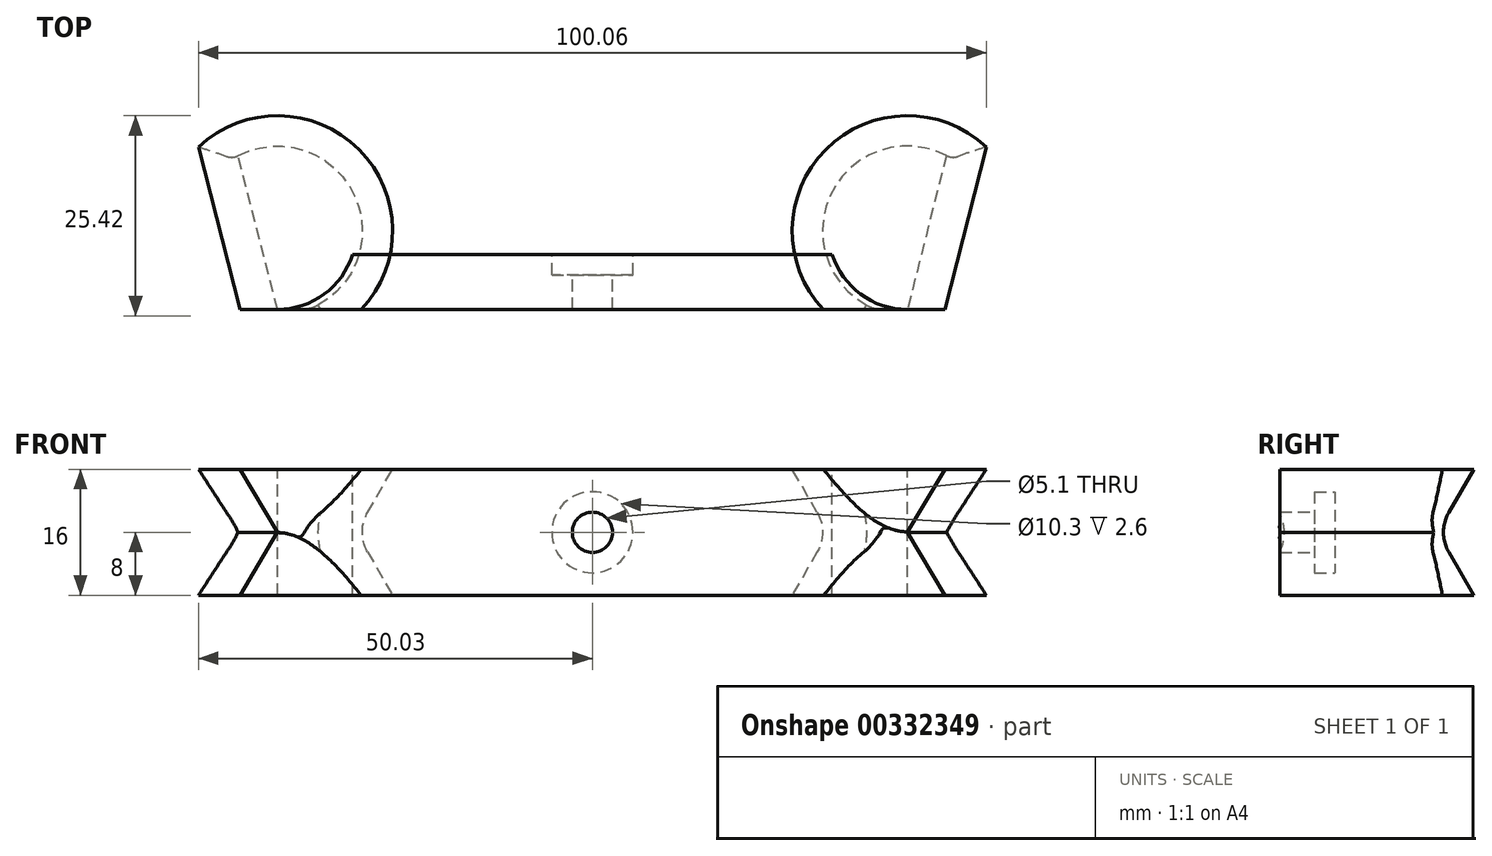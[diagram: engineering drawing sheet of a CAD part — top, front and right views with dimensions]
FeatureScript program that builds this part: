
annotation { "Feature Type Name" : "Feature", "Feature Type Description" : "" }
export const myFeature = defineFeature(function(context is Context, id is Id, definition is map)
    precondition{}
    {
        {
            var Q0;
            Q0=qCreatedBy(makeId("Top.planeOp"),FACE);
            var sketch = newSketch(context, id + "F0", { "sketchPlane" : qUnion([Q0])});
            skCircle(sketch, "E0", {"center": v(-40, 0) * mm, "radius": 10 * mm});
            skLineSegment(sketch, "E1", {"start": v(-30.46, -3) * mm, "end": v(0, -3) * mm});
            skLineSegment(sketch, "E2", {"start": v(-40, -10) * mm, "end": v(0, -10) * mm});
            skLineSegment(sketch, "E3", {"start": v(-40, -10) * mm, "end": v(-44.8, 8.78) * mm});
            skLineSegment(sketch, "E4.MirrorCS", {"start": v(30.46, -3) * mm, "end": v(0, -3) * mm});
            skLineSegment(sketch, "E5.MirrorCS", {"start": v(40, -10) * mm, "end": v(44.8, 8.78) * mm});
            skCircle(sketch, "E6.MirrorC", {"center": v(40, 0) * mm, "radius": 10 * mm});
            skLineSegment(sketch, "E7.MirrorCS", {"start": v(40, -10) * mm, "end": v(0, -10) * mm});
            skSolve(sketch);
        }
        {
            var Q0;
            {var subQ2=sQuery(id+"F0.wireOp",EDGE,"E3");Q0=makeQuery(id+"F0.imprint","IMPRINT",FACE,{"disambiguationData":[TD([[makeQuery(id+"F0.imprint","IMPRINT",EDGE,{"derivedFrom":subQ2}),-1.0]])]});}
            var Q1;
            {var subQ0=sQuery(id+"F0.wireOp",EDGE,"E5.MirrorCS");Q1=makeQuery(id+"F0.imprint","IMPRINT",FACE,{"disambiguationData":[TD([[makeQuery(id+"F0.imprint","IMPRINT",EDGE,{"derivedFrom":subQ0}),1.0]])]});}
            extrude(context, id + "F1", {"entities" : qUnion([Q0, Q1]), "depth" : 8 * mm, "offsetDistance" : 25 * mm, "hasDraft" : true, "draftAngle" : 30 * degree, "hasSecondDirection" : true, "secondDirectionOppositeDirection" : true, "secondDirectionDepth" : 8 * mm, "hasSecondDirectionDraft" : true, "secondDirectionDraftAngle" : 30 * degree});
        }
        {
            var Q0;
            {var subQ4=sQuery(id+"F0.wireOp",EDGE,"E1");Q0=makeQuery(id+"F0.imprint","IMPRINT",FACE,{"disambiguationData":[TD([[makeQuery(id+"F0.imprint","IMPRINT",EDGE,{"derivedFrom":subQ4}),-1.0]])]});}
            extrude(context, id + "F2", {"entities" : qUnion([Q0]), "oppositeDirection" : true, "depth" : 8 * mm, "offsetDistance" : 25 * mm, "hasSecondDirection" : true, "secondDirectionOppositeDirection" : false, "secondDirectionDepth" : 8 * mm});
        }
        {
            var Q0;
            Q0=qCreatedBy(makeId("Top.planeOp"),FACE);
            var sketch = newSketch(context, id + "F3", { "sketchPlane" : qUnion([Q0])});
            skLineSegment(sketch, "E8.bottom", {"start": v(-55.61, -28.96) * mm, "end": v(55.9, -28.96) * mm});
            skLineSegment(sketch, "E8.top", {"start": v(-55.61, -10.03) * mm, "end": v(55.9, -10.03) * mm});
            skLineSegment(sketch, "E8.left", {"start": v(-55.61, -28.96) * mm, "end": v(-55.61, -10.03) * mm});
            skLineSegment(sketch, "E8.right", {"start": v(55.9, -28.96) * mm, "end": v(55.9, -10.03) * mm});
            skSolve(sketch);
        }
        {
            var Q0;
            Q0=makeQuery(id+"F3.imprint","IMPRINT",FACE,{"disambiguationData":[TD([[makeQuery(id+"F3.imprint","IMPRINT",EDGE,{"derivedFrom":sQuery(id+"F3.wireOp",EDGE,"E8.bottom")}),1.0]])]});
            extrude(context, id + "F4", {"entities" : qUnion([Q0]), "operationType" : NewBodyOperationType.REMOVE, "depth" : 25 * mm, "offsetDistance" : 25 * mm, "hasSecondDirection" : true, "secondDirectionOppositeDirection" : true, "secondDirectionDepth" : 25 * mm});
        }
        {
            var Q0;
            Q0=makeQuery(id+"F2.opExtrude","SWEPT_FACE",FACE,{"disambiguationData":[OSD([sQuery(id+"F0.wireOp",EDGE,"E1"),sQuery(id+"F0.wireOp",EDGE,"E4.MirrorCS")])]});
            var sketch = newSketch(context, id + "F5", { "sketchPlane" : qUnion([Q0])});
            skCircle(sketch, "E9", {"center": v(0, 0) * mm, "radius": 5.15 * mm});
            skCircle(sketch, "E10", {"center": v(0, 0) * mm, "radius": 2.55 * mm});
            skSolve(sketch);
        }
        {
            var Q0;
            Q0=makeQuery(id+"F5.imprint","IMPRINT",FACE,{"disambiguationData":[TD([[makeQuery(id+"F5.imprint","IMPRINT",EDGE,{"derivedFrom":sQuery(id+"F5.wireOp",EDGE,"E10")}),1.0]])]});
            extrude(context, id + "F6", {"entities" : qUnion([Q0]), "operationType" : NewBodyOperationType.REMOVE, "oppositeDirection" : true, "depth" : 25 * mm, "offsetDistance" : 25 * mm});
        }
        {
            var Q0;
            Q0=makeQuery(id+"F5.imprint","IMPRINT",FACE,{"disambiguationData":[TD([[makeQuery(id+"F5.imprint","IMPRINT",EDGE,{"derivedFrom":sQuery(id+"F5.wireOp",EDGE,"E9")}),1.0]])]});
            extrude(context, id + "F7", {"entities" : qUnion([Q0]), "operationType" : NewBodyOperationType.REMOVE, "oppositeDirection" : true, "depth" : 2.6 * mm, "offsetDistance" : 25 * mm});
        }
        {
            var Q0;
            {var subQ0=makeQuery(id+"F1.opExtrude","SWEPT_FACE",FACE,{"disambiguationData":[OSD([sQuery(id+"F0.wireOp",EDGE,"E0")])]});Q0=makeQuery(id+"F1.*.booleanUnion.opBoolean","MERGE",EDGE,{"derivedFrom":[makeQuery(id+"F1.*.split.splitOp","SPLIT_SURFACE_INTERSECT",EDGE,{"derivedFrom":[subQ0]}),makeQuery(id+"F1.*.split.splitOp","SPLIT_SURFACE_INTERSECT",EDGE,{"derivedFrom":[subQ0],"isFromBackBody":true})]});}
            var Q1;
            {var subQ0=makeQuery(id+"F1.opExtrude","SWEPT_FACE",FACE,{"disambiguationData":[OSD([sQuery(id+"F0.wireOp",EDGE,"E6.MirrorC")])]});Q1=makeQuery(id+"F1.*.booleanUnion.opBoolean","MERGE",EDGE,{"derivedFrom":[makeQuery(id+"F1.*.split.splitOp","SPLIT_SURFACE_INTERSECT",EDGE,{"derivedFrom":[subQ0]}),makeQuery(id+"F1.*.split.splitOp","SPLIT_SURFACE_INTERSECT",EDGE,{"derivedFrom":[subQ0],"isFromBackBody":true})]});}
            fillet(context, id + "F8", {"entities" : qUnion([Q0, Q1]), "tangentPropagation" : true, "radius" : 5 * mm, "defaultsChanged" : false, "vertexSettings" : [], "allowEdgeOverflow" : false});
        }
    });
